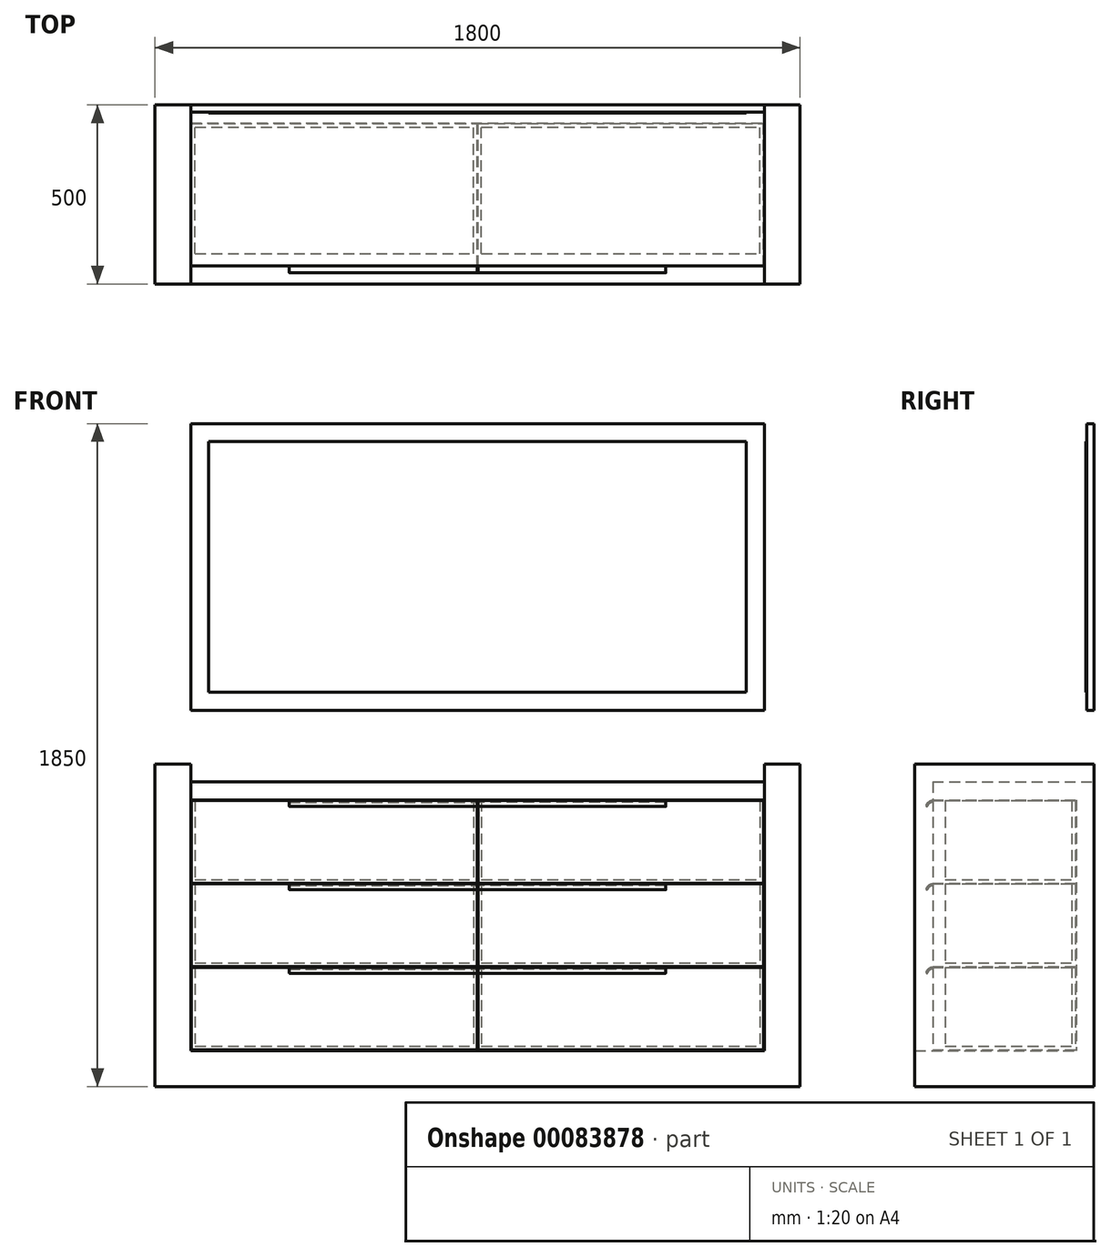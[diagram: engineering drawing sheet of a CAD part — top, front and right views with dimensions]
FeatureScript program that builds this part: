
annotation { "Feature Type Name" : "Feature", "Feature Type Description" : "" }
export const myFeature = defineFeature(function(context is Context, id is Id, definition is map)
    precondition{}
    {
        {
            assignVariable(context, id + "F0", {"name" : "GoldenRatio", "anyValue" : 1.62});
        }
        {
            assignVariable(context, id + "F1", {"name" : "Width", "anyValue" : 1800 * mm});
        }
        {
            assignVariable(context, id + "F2", {"name" : "Depth", "anyValue" : 500 * mm});
        }
        {
            assignVariable(context, id + "F3", {"name" : "Thickness1", "anyValue" : 100 * mm});
        }
        {
            assignVariable(context, id + "F4", {"name" : "Thickness2", "anyValue" : 50 * mm});
        }
        {
            assignVariable(context, id + "F5", {"name" : "Thickness3", "anyValue" : 10 * mm});
        }
        {
            assignVariable(context, id + "F6", {"name" : "Margin", "anyValue" : 2 * mm});
        }
        {
            assignVariable(context, id + "F7", {"name" : "HandleLengthFraction", "anyValue" : getVariable(context, 'GoldenRatio') / (1 + getVariable(context, 'GoldenRatio'))});
        }
        {
            var Q0;
            Q0=qCreatedBy(makeId("Front.planeOp"),FACE);
            var sketch = newSketch(context, id + "F8", { "sketchPlane" : qUnion([Q0])});
            skLineSegment(sketch, "E0.top", {"start": v(-900, 0) * mm, "end": v(900, 0) * mm});
            skLineSegment(sketch, "E0.left", {"start": v(-900, 900) * mm, "end": v(-900, 0) * mm});
            skLineSegment(sketch, "E0.right", {"start": v(900, 900) * mm, "end": v(900, 0) * mm});
            skLineSegment(sketch, "E1", {"start": v(-900, 900) * mm, "end": v(-800, 900) * mm});
            skLineSegment(sketch, "E2", {"start": v(-800, 900) * mm, "end": v(-800, 850) * mm});
            skLineSegment(sketch, "E3", {"start": v(800, 850) * mm, "end": v(800, 900) * mm});
            skLineSegment(sketch, "E4", {"start": v(800, 900) * mm, "end": v(900, 900) * mm});
            skLineSegment(sketch, "E5.bottom", {"start": v(-800, 850) * mm, "end": v(800, 850) * mm});
            skLineSegment(sketch, "E5.top", {"start": v(-800, 800) * mm, "end": v(800, 800) * mm});
            skLineSegment(sketch, "E5.left", {"start": v(-800, 850) * mm, "end": v(-800, 800) * mm});
            skLineSegment(sketch, "E5.right", {"start": v(800, 850) * mm, "end": v(800, 800) * mm});
            skLineSegment(sketch, "E6.top", {"start": v(-800, 100) * mm, "end": v(800, 100) * mm});
            skLineSegment(sketch, "E6.left", {"start": v(-800, 800) * mm, "end": v(-800, 100) * mm});
            skLineSegment(sketch, "E6.right", {"start": v(800, 800) * mm, "end": v(800, 100) * mm});
            skLineSegment(sketch, "E7.bottom", {"start": v(-798, 798) * mm, "end": v(-1, 798) * mm});
            skLineSegment(sketch, "E7.top", {"start": v(-798, 567.33) * mm, "end": v(-1, 567.33) * mm});
            skLineSegment(sketch, "E7.left", {"start": v(-798, 798) * mm, "end": v(-798, 567.33) * mm});
            skLineSegment(sketch, "E7.right", {"start": v(798, 798) * mm, "end": v(798, 567.33) * mm});
            skLineSegment(sketch, "E8.bottom", {"start": v(-798, 565.33) * mm, "end": v(-1, 565.33) * mm});
            skLineSegment(sketch, "E8.top", {"start": v(-798, 334.67) * mm, "end": v(-1, 334.67) * mm});
            skLineSegment(sketch, "E8.left", {"start": v(-798, 565.33) * mm, "end": v(-798, 334.67) * mm});
            skLineSegment(sketch, "E8.right", {"start": v(798, 565.33) * mm, "end": v(798, 334.67) * mm});
            skLineSegment(sketch, "E9.bottom", {"start": v(-798, 332.67) * mm, "end": v(-1, 332.67) * mm});
            skLineSegment(sketch, "E9.top", {"start": v(-798, 102) * mm, "end": v(-1, 102) * mm});
            skLineSegment(sketch, "E9.left", {"start": v(-798, 332.67) * mm, "end": v(-798, 102) * mm});
            skLineSegment(sketch, "E9.right", {"start": v(798, 332.67) * mm, "end": v(798, 102) * mm});
            skLineSegment(sketch, "E10", {"start": v(-1, 798) * mm, "end": v(-1, 567.33) * mm});
            skLineSegment(sketch, "E11", {"start": v(-1, 565.33) * mm, "end": v(-1, 334.67) * mm});
            skLineSegment(sketch, "E12", {"start": v(-1, 332.67) * mm, "end": v(-1, 102) * mm});
            skLineSegment(sketch, "E13", {"start": v(1, 798) * mm, "end": v(1, 567.33) * mm});
            skLineSegment(sketch, "E14", {"start": v(1, 565.33) * mm, "end": v(1, 334.67) * mm});
            skLineSegment(sketch, "E15", {"start": v(1, 332.67) * mm, "end": v(1, 102) * mm});
            skLineSegment(sketch, "E16.trimOffspring", {"start": v(1, 798) * mm, "end": v(798, 798) * mm});
            skLineSegment(sketch, "E17.trimOffspring", {"start": v(1, 567.33) * mm, "end": v(798, 567.33) * mm});
            skLineSegment(sketch, "E18.trimOffspring", {"start": v(1, 565.33) * mm, "end": v(798, 565.33) * mm});
            skLineSegment(sketch, "E19.trimOffspring", {"start": v(1, 334.67) * mm, "end": v(798, 334.67) * mm});
            skLineSegment(sketch, "E20.trimOffspring", {"start": v(1, 332.67) * mm, "end": v(798, 332.67) * mm});
            skLineSegment(sketch, "E21.trimOffspring", {"start": v(1, 102) * mm, "end": v(798, 102) * mm});
            skLineSegment(sketch, "E22.bottom", {"start": v(-800, 1850) * mm, "end": v(800, 1850) * mm});
            skLineSegment(sketch, "E22.top", {"start": v(-800, 1050) * mm, "end": v(800, 1050) * mm});
            skLineSegment(sketch, "E22.left", {"start": v(-800, 1850) * mm, "end": v(-800, 1050) * mm});
            skLineSegment(sketch, "E22.right", {"start": v(800, 1850) * mm, "end": v(800, 1050) * mm});
            skLineSegment(sketch, "E23.0", {"start": v(-750, 1800) * mm, "end": v(750, 1800) * mm});
            skLineSegment(sketch, "E23.1", {"start": v(-750, 1800) * mm, "end": v(-750, 1100) * mm});
            skLineSegment(sketch, "E23.2", {"start": v(-750, 1100) * mm, "end": v(750, 1100) * mm});
            skLineSegment(sketch, "E23.3", {"start": v(750, 1800) * mm, "end": v(750, 1100) * mm});
            skSolve(sketch);
        }
        {
            var Q0;
            Q0=makeQuery(id+"F8.imprint","IMPRINT",FACE,{"disambiguationData":[TD([[makeQuery(id+"F8.imprint","IMPRINT",EDGE,{"derivedFrom":sQuery(id+"F8.wireOp",EDGE,"E0.top")}),1.0]])]});
            extrude(context, id + "F9", {"entities" : qUnion([Q0]), "depth" : getVariable(context, 'Depth')});
        }
        {
            var Q0;
            Q0=makeQuery(id+"F8.imprint","IMPRINT",FACE,{"disambiguationData":[TD([[makeQuery(id+"F8.imprint","IMPRINT",EDGE,{"derivedFrom":sQuery(id+"F8.wireOp",EDGE,"E5.bottom")}),-1.0]])]});
            extrude(context, id + "F10", {"entities" : qUnion([Q0]), "operationType" : NewBodyOperationType.ADD, "depth" : getVariable(context, 'Depth') - getVariable(context, 'Thickness2')});
        }
        {
            var Q0;
            Q0=makeQuery(id+"F8.imprint","IMPRINT",FACE,{"disambiguationData":[TD([[makeQuery(id+"F8.imprint","IMPRINT",EDGE,{"derivedFrom":sQuery(id+"F8.wireOp",EDGE,"E5.top")}),-1.0]])]});
            var Q1;
            Q1=makeQuery(id+"F8.imprint","IMPRINT",FACE,{"disambiguationData":[TD([[makeQuery(id+"F8.imprint","IMPRINT",EDGE,{"derivedFrom":sQuery(id+"F8.wireOp",EDGE,"E7.bottom")}),-1.0]])]});
            var Q2;
            Q2=makeQuery(id+"F8.imprint","IMPRINT",FACE,{"disambiguationData":[TD([[makeQuery(id+"F8.imprint","IMPRINT",EDGE,{"derivedFrom":sQuery(id+"F8.wireOp",EDGE,"E8.bottom")}),-1.0]])]});
            var Q3;
            Q3=makeQuery(id+"F8.imprint","IMPRINT",FACE,{"disambiguationData":[TD([[makeQuery(id+"F8.imprint","IMPRINT",EDGE,{"derivedFrom":sQuery(id+"F8.wireOp",EDGE,"E9.bottom")}),-1.0]])]});
            var Q4;
            Q4=makeQuery(id+"F8.imprint","IMPRINT",FACE,{"disambiguationData":[TD([[makeQuery(id+"F8.imprint","IMPRINT",EDGE,{"derivedFrom":sQuery(id+"F8.wireOp",EDGE,"E7.right")}),-1.0]])]});
            var Q5;
            Q5=makeQuery(id+"F8.imprint","IMPRINT",FACE,{"disambiguationData":[TD([[makeQuery(id+"F8.imprint","IMPRINT",EDGE,{"derivedFrom":sQuery(id+"F8.wireOp",EDGE,"E8.right")}),-1.0]])]});
            var Q6;
            Q6=makeQuery(id+"F8.imprint","IMPRINT",FACE,{"disambiguationData":[TD([[makeQuery(id+"F8.imprint","IMPRINT",EDGE,{"derivedFrom":sQuery(id+"F8.wireOp",EDGE,"E9.right")}),-1.0]])]});
            extrude(context, id + "F11", {"entities" : qUnion([Q0, Q1, Q2, Q3, Q4, Q5, Q6]), "operationType" : NewBodyOperationType.ADD, "depth" : getVariable(context, 'Thickness2')});
        }
        {
            var Q0;
            Q0=makeQuery(id+"F8.imprint","IMPRINT",FACE,{"disambiguationData":[TD([[makeQuery(id+"F8.imprint","IMPRINT",EDGE,{"derivedFrom":sQuery(id+"F8.wireOp",EDGE,"E7.bottom")}),-1.0]])]});
            var Q1;
            Q1=makeQuery(id+"F8.imprint","IMPRINT",FACE,{"disambiguationData":[TD([[makeQuery(id+"F8.imprint","IMPRINT",EDGE,{"derivedFrom":sQuery(id+"F8.wireOp",EDGE,"E7.right")}),-1.0]])]});
            var Q2;
            Q2=makeQuery(id+"F8.imprint","IMPRINT",FACE,{"disambiguationData":[TD([[makeQuery(id+"F8.imprint","IMPRINT",EDGE,{"derivedFrom":sQuery(id+"F8.wireOp",EDGE,"E8.bottom")}),-1.0]])]});
            var Q3;
            Q3=makeQuery(id+"F8.imprint","IMPRINT",FACE,{"disambiguationData":[TD([[makeQuery(id+"F8.imprint","IMPRINT",EDGE,{"derivedFrom":sQuery(id+"F8.wireOp",EDGE,"E8.right")}),-1.0]])]});
            var Q4;
            Q4=makeQuery(id+"F8.imprint","IMPRINT",FACE,{"disambiguationData":[TD([[makeQuery(id+"F8.imprint","IMPRINT",EDGE,{"derivedFrom":sQuery(id+"F8.wireOp",EDGE,"E9.bottom")}),-1.0]])]});
            var Q5;
            Q5=makeQuery(id+"F8.imprint","IMPRINT",FACE,{"disambiguationData":[TD([[makeQuery(id+"F8.imprint","IMPRINT",EDGE,{"derivedFrom":sQuery(id+"F8.wireOp",EDGE,"E9.right")}),-1.0]])]});
            extrude(context, id + "F12", {"entities" : qUnion([Q0, Q1, Q2, Q3, Q4, Q5]), "depth" : getVariable(context, 'Depth') - getVariable(context, 'Thickness2'), "hasSecondDirection" : true, "secondDirectionOppositeDirection" : false, "secondDirectionDepth" : getVariable(context, 'Thickness2') + getVariable(context, 'Margin')});
        }
        {
            var Q0;
            Q0=makeQuery(id+"F12.opExtrude","SWEPT_FACE",FACE,{"disambiguationData":[OSD([sQuery(id+"F8.wireOp",EDGE,"E16.trimOffspring")])]});
            var Q1;
            Q1=makeQuery(id+"F12.opExtrude","SWEPT_FACE",FACE,{"disambiguationData":[OSD([sQuery(id+"F8.wireOp",EDGE,"E7.bottom")])]});
            var Q2;
            Q2=makeQuery(id+"F12.opExtrude","SWEPT_FACE",FACE,{"disambiguationData":[OSD([sQuery(id+"F8.wireOp",EDGE,"E18.trimOffspring")])]});
            var Q3;
            Q3=makeQuery(id+"F12.opExtrude","SWEPT_FACE",FACE,{"disambiguationData":[OSD([sQuery(id+"F8.wireOp",EDGE,"E8.bottom")])]});
            var Q4;
            Q4=makeQuery(id+"F12.opExtrude","SWEPT_FACE",FACE,{"disambiguationData":[OSD([sQuery(id+"F8.wireOp",EDGE,"E20.trimOffspring")])]});
            var Q5;
            Q5=makeQuery(id+"F12.opExtrude","SWEPT_FACE",FACE,{"disambiguationData":[OSD([sQuery(id+"F8.wireOp",EDGE,"E9.bottom")])]});
            shell(context, id + "F13", {"entities" : qUnion([Q0, Q1, Q2, Q3, Q4, Q5]), "thickness" : getVariable(context, 'Thickness3')});
        }
        {
            var Q0;
            {var subQ0=sQuery(id+"F8.wireOp",EDGE,"E10");var subQ1=sQuery(id+"F8.wireOp",EDGE,"E7.left");var subQ2=sQuery(id+"F8.wireOp",EDGE,"E7.top");var subQ3=sQuery(id+"F8.wireOp",EDGE,"E7.bottom");Q0=makeQuery(id+"F13.opShell","OFFSET_FACE",FACE,{"disambiguationData":[OSD([subQ3,subQ2,subQ1,subQ0]),TDD([makeQuery(id+"F12.opExtrude","CAP_FACE",FACE,{"disambiguationData":[OSD([subQ3,subQ2,subQ1,subQ0])],"isStart":false})])]});}
            var Q1;
            {var subQ0=sQuery(id+"F8.wireOp",EDGE,"E17.trimOffspring");var subQ1=sQuery(id+"F8.wireOp",EDGE,"E16.trimOffspring");var subQ2=sQuery(id+"F8.wireOp",EDGE,"E13");var subQ3=sQuery(id+"F8.wireOp",EDGE,"E7.right");Q1=makeQuery(id+"F13.opShell","OFFSET_FACE",FACE,{"disambiguationData":[OSD([subQ3,subQ2,subQ1,subQ0]),TDD([makeQuery(id+"F12.opExtrude","CAP_FACE",FACE,{"disambiguationData":[OSD([subQ3,subQ2,subQ1,subQ0])],"isStart":false})])]});}
            var Q2;
            {var subQ0=sQuery(id+"F8.wireOp",EDGE,"E11");var subQ1=sQuery(id+"F8.wireOp",EDGE,"E8.left");var subQ2=sQuery(id+"F8.wireOp",EDGE,"E8.top");var subQ3=sQuery(id+"F8.wireOp",EDGE,"E8.bottom");Q2=makeQuery(id+"F13.opShell","OFFSET_FACE",FACE,{"disambiguationData":[OSD([subQ3,subQ2,subQ1,subQ0]),TDD([makeQuery(id+"F12.opExtrude","CAP_FACE",FACE,{"disambiguationData":[OSD([subQ3,subQ2,subQ1,subQ0])],"isStart":false})])]});}
            var Q3;
            {var subQ0=sQuery(id+"F8.wireOp",EDGE,"E19.trimOffspring");var subQ1=sQuery(id+"F8.wireOp",EDGE,"E18.trimOffspring");var subQ2=sQuery(id+"F8.wireOp",EDGE,"E14");var subQ3=sQuery(id+"F8.wireOp",EDGE,"E8.right");Q3=makeQuery(id+"F13.opShell","OFFSET_FACE",FACE,{"disambiguationData":[OSD([subQ3,subQ2,subQ1,subQ0]),TDD([makeQuery(id+"F12.opExtrude","CAP_FACE",FACE,{"disambiguationData":[OSD([subQ3,subQ2,subQ1,subQ0])],"isStart":false})])]});}
            var Q4;
            {var subQ0=sQuery(id+"F8.wireOp",EDGE,"E12");var subQ1=sQuery(id+"F8.wireOp",EDGE,"E9.left");var subQ2=sQuery(id+"F8.wireOp",EDGE,"E9.top");var subQ3=sQuery(id+"F8.wireOp",EDGE,"E9.bottom");Q4=makeQuery(id+"F13.opShell","OFFSET_FACE",FACE,{"disambiguationData":[OSD([subQ3,subQ2,subQ1,subQ0]),TDD([makeQuery(id+"F12.opExtrude","CAP_FACE",FACE,{"disambiguationData":[OSD([subQ3,subQ2,subQ1,subQ0])],"isStart":false})])]});}
            var Q5;
            {var subQ0=sQuery(id+"F8.wireOp",EDGE,"E21.trimOffspring");var subQ1=sQuery(id+"F8.wireOp",EDGE,"E20.trimOffspring");var subQ2=sQuery(id+"F8.wireOp",EDGE,"E15");var subQ3=sQuery(id+"F8.wireOp",EDGE,"E9.right");Q5=makeQuery(id+"F13.opShell","OFFSET_FACE",FACE,{"disambiguationData":[OSD([subQ3,subQ2,subQ1,subQ0]),TDD([makeQuery(id+"F12.opExtrude","CAP_FACE",FACE,{"disambiguationData":[OSD([subQ3,subQ2,subQ1,subQ0])],"isStart":false})])]});}
            extrude(context, id + "F14", {"entities" : qUnion([Q0, Q1, Q2, Q3, Q4, Q5]), "operationType" : NewBodyOperationType.ADD, "depth" : 25 * mm});
        }
        {
            var Q0;
            Q0=qCreatedBy(makeId("Right.planeOp"),FACE);
            var sketch = newSketch(context, id + "F15", { "sketchPlane" : qUnion([Q0])});
            skArc(sketch, "E24", {"start": v(-450, 798) * mm, "mid": v(-461.47, 794.38) * mm, "end": v(-468.8, 784.84) * mm});
            skArc(sketch, "E25", {"start": v(-450, 793) * mm, "mid": v(-458.6, 790.29) * mm, "end": v(-464.1, 783.13) * mm});
            skArc(sketch, "E26", {"start": v(-468.8, 784.84) * mm, "mid": v(-467.3, 781.64) * mm, "end": v(-464.1, 783.13) * mm});
            skLineSegment(sketch, "E27", {"start": v(-466.44, 783.99) * mm, "end": v(-450, 778) * mm, "construction": true});
            skLineSegment(sketch, "E28", {"start": v(-450, 793) * mm, "end": v(-450, 798) * mm});
            skArc(sketch, "E29.1.0.0", {"start": v(-450, 565.33) * mm, "mid": v(-461.47, 561.72) * mm, "end": v(-468.8, 552.17) * mm});
            skArc(sketch, "E29.1.0.1", {"start": v(-450, 560.33) * mm, "mid": v(-458.6, 557.62) * mm, "end": v(-464.1, 550.46) * mm});
            skLineSegment(sketch, "E29.1.0.2", {"start": v(-450, 560.33) * mm, "end": v(-450, 565.33) * mm});
            skArc(sketch, "E29.1.0.3", {"start": v(-468.8, 552.17) * mm, "mid": v(-467.3, 548.97) * mm, "end": v(-464.1, 550.46) * mm});
            skArc(sketch, "E29.2.0.0", {"start": v(-450, 332.67) * mm, "mid": v(-461.47, 329.05) * mm, "end": v(-468.8, 319.5) * mm});
            skArc(sketch, "E29.2.0.1", {"start": v(-450, 327.67) * mm, "mid": v(-458.6, 324.95) * mm, "end": v(-464.1, 317.8) * mm});
            skLineSegment(sketch, "E29.2.0.2", {"start": v(-450, 327.67) * mm, "end": v(-450, 332.67) * mm});
            skArc(sketch, "E29.2.0.3", {"start": v(-468.8, 319.5) * mm, "mid": v(-467.3, 316.3) * mm, "end": v(-464.1, 317.8) * mm});
            skLineSegment(sketch, "E29.direction1", {"start": v(-468.8, 784.84) * mm, "end": v(-468.8, 552.17) * mm, "construction": true});
            skSolve(sketch);
        }
        {
            var Q0;
            Q0 = qSketchRegion(id + "F15", true);
            extrude(context, id + "F16", {"entities" : qUnion([Q0]), "depth" : getVariable(context, 'HandleLengthFraction') * (getVariable(context, 'Width') - getVariable(context, 'Thickness1')) / 2, "hasSecondDirection" : true, "secondDirectionOppositeDirection" : false, "secondDirectionDepth" : getVariable(context, 'Margin') / 2});
        }
        {
            var Q0;
            Q0=makeQuery(id+"F16.opExtrude","SWEPT_BODY",BODY,{"disambiguationData":[OSD([sQuery(id+"F15.wireOp",EDGE,"E24"),sQuery(id+"F15.wireOp",EDGE,"E25"),sQuery(id+"F15.wireOp",EDGE,"E26"),sQuery(id+"F15.wireOp",EDGE,"E28")])]});
            var Q1;
            Q1=makeQuery(id+"F16.opExtrude","SWEPT_BODY",BODY,{"disambiguationData":[OSD([sQuery(id+"F15.wireOp",EDGE,"E29.1.0.0"),sQuery(id+"F15.wireOp",EDGE,"E29.1.0.1"),sQuery(id+"F15.wireOp",EDGE,"E29.1.0.2"),sQuery(id+"F15.wireOp",EDGE,"E29.1.0.3")])]});
            var Q2;
            Q2=makeQuery(id+"F16.opExtrude","SWEPT_BODY",BODY,{"disambiguationData":[OSD([sQuery(id+"F15.wireOp",EDGE,"E29.2.0.0"),sQuery(id+"F15.wireOp",EDGE,"E29.2.0.1"),sQuery(id+"F15.wireOp",EDGE,"E29.2.0.2"),sQuery(id+"F15.wireOp",EDGE,"E29.2.0.3")])]});
            var Q3;
            Q3=qCreatedBy(makeId("Right.planeOp"),FACE);
            mirror(context, id + "F17", {"entities" : qUnion([Q0, Q1, Q2]), "mirrorPlane" : qUnion([Q3])});
        }
        {
            var Q0;
            Q0=makeQuery(id+"F8.imprint","IMPRINT",FACE,{"disambiguationData":[TD([[makeQuery(id+"F8.imprint","IMPRINT",EDGE,{"derivedFrom":sQuery(id+"F8.wireOp",EDGE,"E22.bottom")}),-1.0]])]});
            var Q1;
            Q1=makeQuery(id+"F8.imprint","IMPRINT",FACE,{"disambiguationData":[TD([[makeQuery(id+"F8.imprint","IMPRINT",EDGE,{"derivedFrom":sQuery(id+"F8.wireOp",EDGE,"E23.0")}),-1.0]])]});
            extrude(context, id + "F18", {"entities" : qUnion([Q0, Q1]), "depth" : 2 * getVariable(context, 'Thickness3')});
        }
        {
            var Q0;
            Q0=makeQuery(id+"F8.imprint","IMPRINT",FACE,{"disambiguationData":[TD([[makeQuery(id+"F8.imprint","IMPRINT",EDGE,{"derivedFrom":sQuery(id+"F8.wireOp",EDGE,"E23.0")}),-1.0]])]});
            extrude(context, id + "F19", {"entities" : qUnion([Q0]), "depth" : 2 * getVariable(context, 'Thickness3') + 3 * mm, "hasSecondDirection" : true, "secondDirectionOppositeDirection" : false, "secondDirectionDepth" : 2 * getVariable(context, 'Thickness3')});
        }
    });
